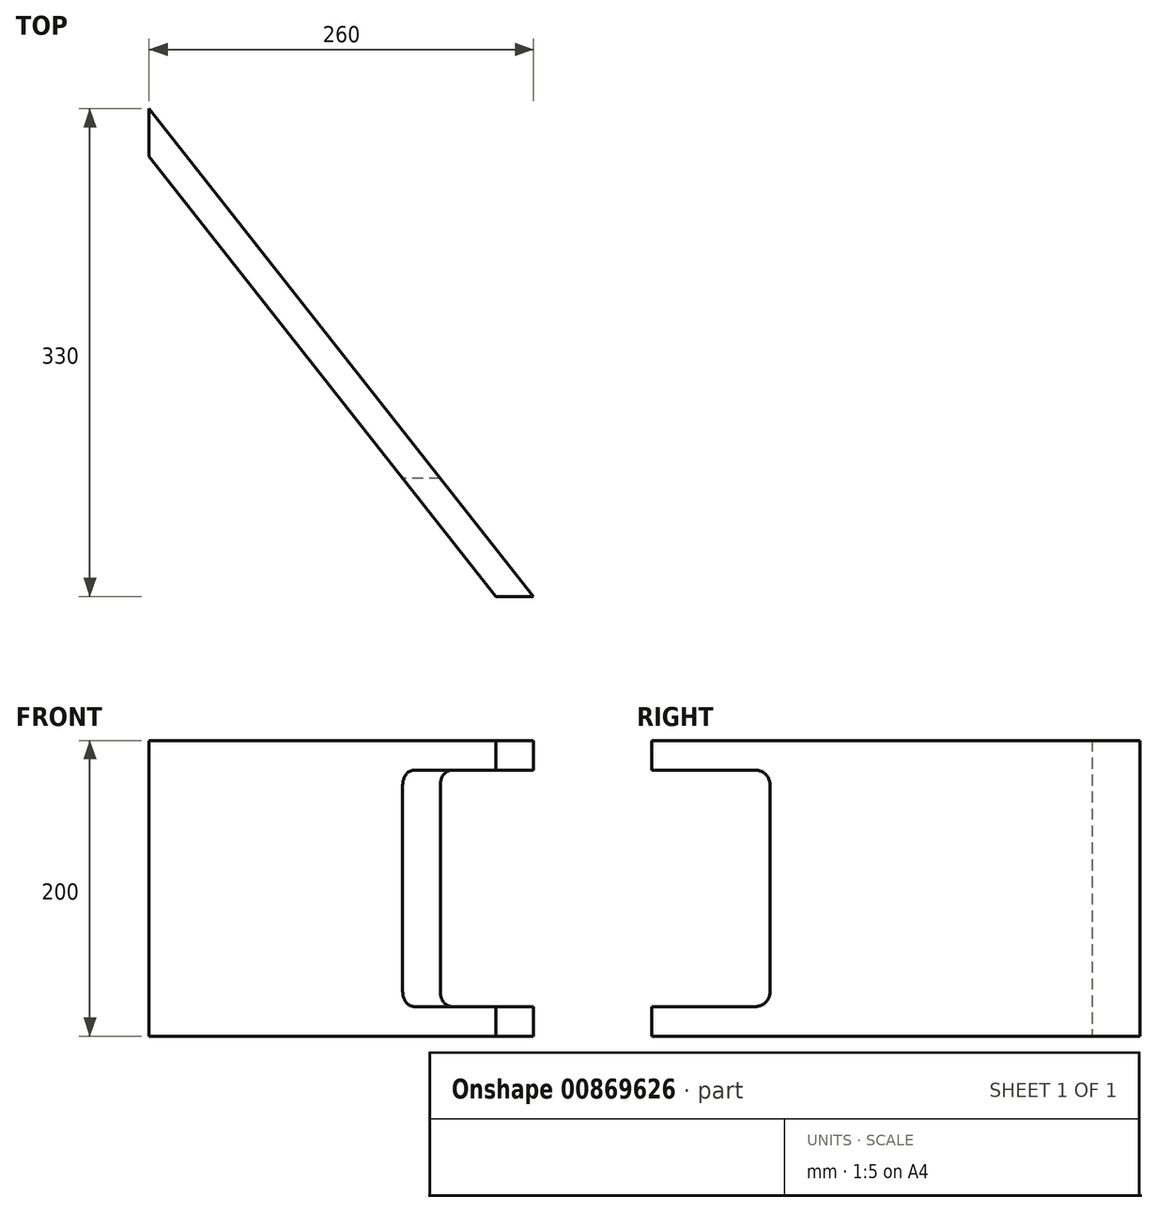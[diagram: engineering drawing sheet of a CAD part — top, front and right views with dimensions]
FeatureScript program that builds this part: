
annotation { "Feature Type Name" : "Feature", "Feature Type Description" : "" }
export const myFeature = defineFeature(function(context is Context, id is Id, definition is map)
    precondition{}
    {
        {
            var Q0;
            Q0=qCreatedBy(makeId("Top.planeOp"),FACE);
            var sketch = newSketch(context, id + "F0", { "sketchPlane" : qUnion([Q0])});
            skLineSegment(sketch, "E0", {"start": v(20, 0) * mm, "end": v(0, 0) * mm});
            skLineSegment(sketch, "E1", {"start": v(0, 0) * mm, "end": v(300, 0) * mm});
            skLineSegment(sketch, "E2", {"start": v(0, 0) * mm, "end": v(0, 330) * mm});
            skLineSegment(sketch, "E3", {"start": v(0, 330) * mm, "end": v(40, 330) * mm});
            skLineSegment(sketch, "E4", {"start": v(40, 330) * mm, "end": v(300, 0) * mm});
            skLineSegment(sketch, "E5", {"start": v(40, 330) * mm, "end": v(40, 297.68) * mm});
            skLineSegment(sketch, "E6", {"start": v(40, 297.68) * mm, "end": v(274.54, 0) * mm});
            skLineSegment(sketch, "E7", {"start": v(274.54, 0) * mm, "end": v(300, 0) * mm});
            skSolve(sketch);
        }
        {
            var Q0;
            Q0=makeQuery(id+"F0.imprint","IMPRINT",FACE,{"disambiguationData":[TD([[makeQuery(id+"F0.imprint","IMPRINT",EDGE,{"derivedFrom":sQuery(id+"F0.wireOp",EDGE,"E4")}),-1.0]])]});
            extrude(context, id + "F1", {"entities" : qUnion([Q0]), "depth" : 200 * mm, "offsetDistance" : 25 * mm});
        }
        {
            var Q0;
            Q0=qCreatedBy(makeId("Right.planeOp"),FACE);
            var sketch = newSketch(context, id + "F2", { "sketchPlane" : qUnion([Q0])});
            skLineSegment(sketch, "E8.bottom", {"start": v(80, 170) * mm, "end": v(80, 30) * mm});
            skLineSegment(sketch, "E8.top", {"start": v(0, 170) * mm, "end": v(0, 30) * mm});
            skLineSegment(sketch, "E8.left", {"start": v(70, 180) * mm, "end": v(10, 180) * mm});
            skLineSegment(sketch, "E8.right", {"start": v(70, 20) * mm, "end": v(10, 20) * mm});
            skPoint(sketch, "E8.middle", {"position": v(40, 100) * mm});
            skPoint(sketch, "E9.visualSharp", {"position": v(0, 20) * mm});
            skArc(sketch, "E9.filletArc", {"start": v(0, 30) * mm, "mid": v(2.93, 22.93) * mm, "end": v(10, 20) * mm});
            skPoint(sketch, "E10.visualSharp", {"position": v(80, 20) * mm});
            skArc(sketch, "E10.filletArc", {"start": v(70, 20) * mm, "mid": v(77.07, 22.93) * mm, "end": v(80, 30) * mm});
            skPoint(sketch, "E11.visualSharp", {"position": v(80, 180) * mm});
            skArc(sketch, "E11.filletArc", {"start": v(80, 170) * mm, "mid": v(77.07, 177.07) * mm, "end": v(70, 180) * mm});
            skPoint(sketch, "E12.visualSharp", {"position": v(0, 180) * mm});
            skArc(sketch, "E12.filletArc", {"start": v(10, 180) * mm, "mid": v(2.93, 177.07) * mm, "end": v(0, 170) * mm});
            skLineSegment(sketch, "E13", {"start": v(0, 0) * mm, "end": v(0, 100) * mm});
            skLineSegment(sketch, "E14", {"start": v(0, 100) * mm, "end": v(40, 100) * mm});
            skLineSegment(sketch, "E15", {"start": v(10, 20) * mm, "end": v(-10.6, 20) * mm});
            skLineSegment(sketch, "E16", {"start": v(-10.6, 20) * mm, "end": v(-10.6, 30) * mm});
            skLineSegment(sketch, "E17", {"start": v(-10.6, 30) * mm, "end": v(0, 30) * mm});
            skLineSegment(sketch, "E18", {"start": v(10, 180) * mm, "end": v(-16.8, 180) * mm});
            skLineSegment(sketch, "E19", {"start": v(-16.8, 180) * mm, "end": v(-16.8, 171.05) * mm});
            skLineSegment(sketch, "E20", {"start": v(-16.8, 171.05) * mm, "end": v(0, 170) * mm});
            skSolve(sketch);
        }
        {
            var Q0;
            {var subQ0=sQuery(id+"F2.wireOp",EDGE,"E9.filletArc");var subQ1=makeQuery(id+"F2.imprint","IMPRINT",EDGE,{"derivedFrom":subQ0});var subQ12=sQuery(id+"F2.wireOp",EDGE,"E12.filletArc");var subQ13=makeQuery(id+"F2.imprint","IMPRINT",EDGE,{"derivedFrom":subQ12});var subQ14=sQuery(id+"F2.wireOp",EDGE,"E16");Q0=qUnion([makeQuery(id+"F2.imprint","IMPRINT",FACE,{"disambiguationData":[TD([[subQ13,-1.0]])]}),makeQuery(id+"F2.imprint","IMPRINT",FACE,{"disambiguationData":[TD([[makeQuery(id+"F2.imprint","IMPRINT",EDGE,{"derivedFrom":subQ14}),-1.0]])]}),makeQuery(id+"F2.imprint","IMPRINT",FACE,{"disambiguationData":[TD([[makeQuery(id+"F2.imprint","IMPRINT",EDGE,{"derivedFrom":sQuery(id+"F2.wireOp",EDGE,"E8.bottom")}),-1.0]])]}),makeQuery(id+"F2.imprint","IMPRINT",FACE,{"disambiguationData":[TD([[subQ1,-1.0]])]})]);}
            extrude(context, id + "F3", {"entities" : qUnion([Q0]), "operationType" : NewBodyOperationType.REMOVE, "depth" : 467 * mm, "offsetDistance" : 25 * mm});
        }
    });
